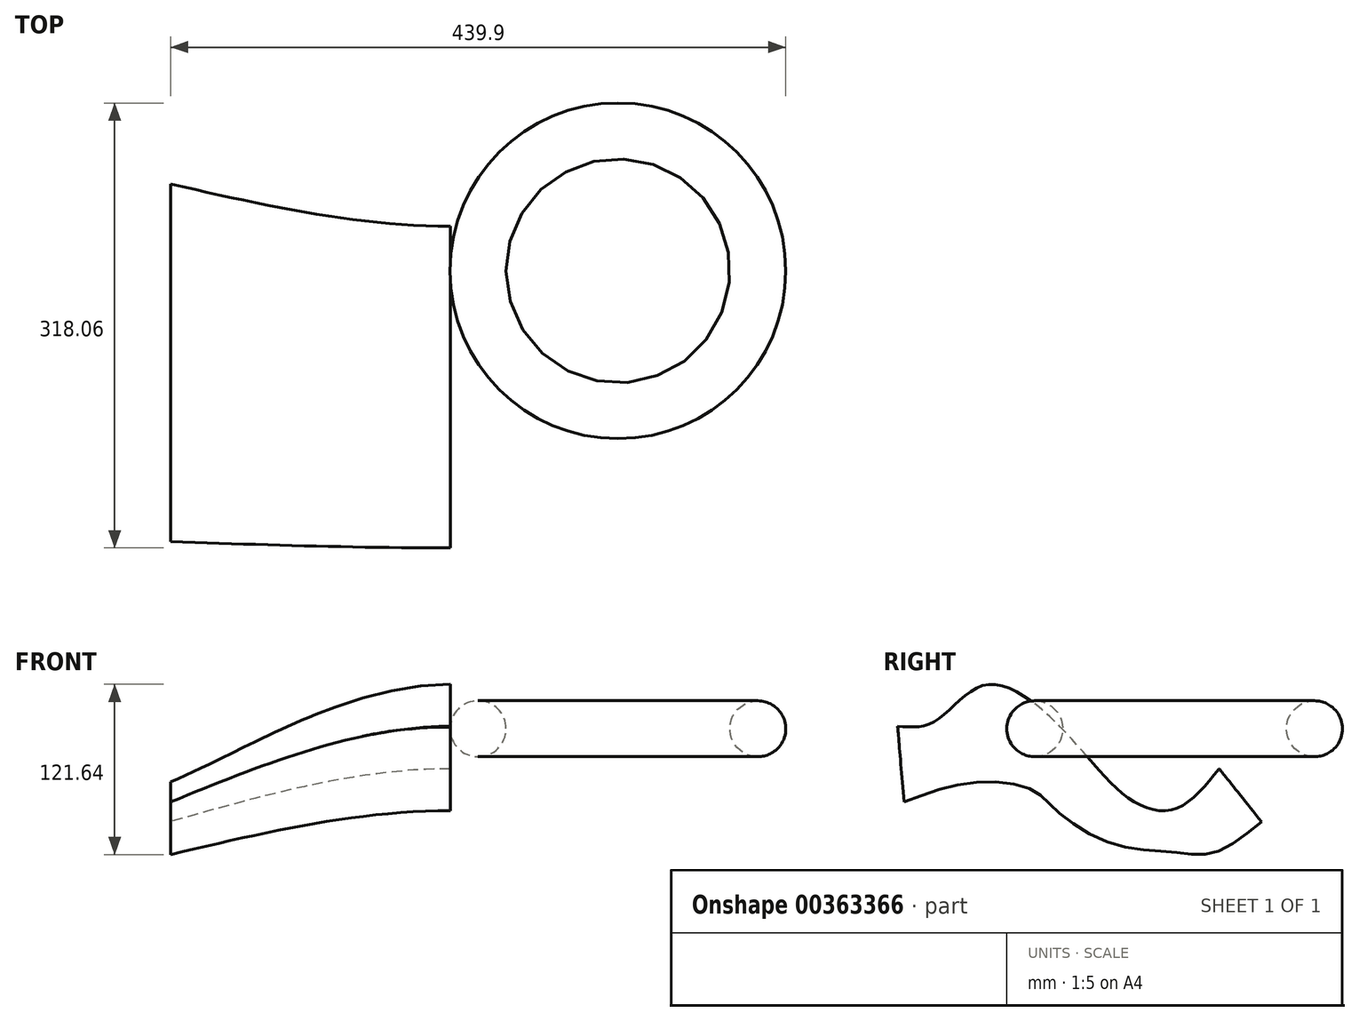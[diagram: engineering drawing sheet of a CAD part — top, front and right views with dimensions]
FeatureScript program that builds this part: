
annotation { "Feature Type Name" : "Feature", "Feature Type Description" : "" }
export const myFeature = defineFeature(function(context is Context, id is Id, definition is map)
    precondition{}
    {
        {
            var Q0;
            Q0=qCreatedBy(makeId("Front.planeOp"),FACE);
            var sketch = newSketch(context, id + "F0", { "sketchPlane" : qUnion([Q0])});
            skLineSegment(sketch, "E0.bottom", {"start": v(-40.1, 58.6) * mm, "end": v(59.9, 58.6) * mm});
            skLineSegment(sketch, "E0.top", {"start": v(-40.1, -6.4) * mm, "end": v(59.9, -6.4) * mm});
            skLineSegment(sketch, "E0.left", {"start": v(-40.1, 58.6) * mm, "end": v(-40.1, -6.4) * mm});
            skLineSegment(sketch, "E0.right", {"start": v(59.9, 58.6) * mm, "end": v(59.9, -6.4) * mm});
            skCircle(sketch, "E1", {"center": v(19.9, 28.6) * mm, "radius": 20 * mm});
            skLineSegment(sketch, "E2", {"start": v(119.9, 79.63) * mm, "end": v(119.9, -11.64) * mm, "construction": true});
            skSolve(sketch);
        }
        {
            var Q0;
            Q0=qCreatedBy(makeId("Right.planeOp"),FACE);
            var sketch = newSketch(context, id + "F1", { "sketchPlane" : qUnion([Q0])});
            skFitSpline(sketch, "E3", {"points": [v(31.85, 0) * mm, v(0, -28.73) * mm, v(-33.26, -20.8) * mm, v(-78.05, 26.03) * mm, v(-134.63, 60.07) * mm, v(-170.83, 34.26) * mm, v(-198.06, 30.31) * mm], "startDerivative": vector(-185.99, -231.7) * mm, "endDerivative": vector(-212.43, 16.55) * mm});
            skSolve(sketch);
        }
        {
            var Q0;
            Q0=sQuery(id+"F0.wireOp",EDGE,"E1");
            var Q1;
            Q1=sQuery(id+"F0.wireOp",EDGE,"E2");
            revolve(context, id + "F2", {"bodyType" : ToolBodyType.SURFACE, "surfaceEntities" : qUnion([Q0]), "axis" : qUnion([Q1]), "revolveType" : RevolveType.FULL});
        }
        {
            var Q0;
            Q0=qCreatedBy(makeId("Right.planeOp"),FACE);
            cPlane(context, id + "F3", {"entities" : qUnion([Q0]), "cplaneType" : CPlaneType.OFFSET, "offset" : 200 * mm, "oppositeDirection" : true, "width" : 150 * mm, "height" : 150 * mm});
        }
        {
            var Q0;
            Q0=qCreatedBy(id+"F3.planeOp",FACE);
            var sketch = newSketch(context, id + "F4", { "sketchPlane" : qUnion([Q0])});
            skFitSpline(sketch, "E4", {"points": [v(-193.53, -23.72) * mm, v(-145.85, -10.13) * mm, v(-101.98, -14.9) * mm, v(-84.1, -30.16) * mm, v(-43.8, -53.76) * mm, v(0, -59.72) * mm, v(27.96, -59.96) * mm, v(62.05, -37.79) * mm], "startDerivative": vector(285.5, 108.3) * mm, "endDerivative": vector(238.04, 195.8) * mm});
            skSolve(sketch);
        }
        {
            var Q0;
            Q0=sQuery(id+"F1.wireOp",EDGE,"E3");
            var Q1;
            Q1=sQuery(id+"F4.wireOp",EDGE,"E4");
            loft(context, id + "F5", {"bodyType" : ToolBodyType.SURFACE, "startCondition" : LoftEndDerivativeType.NORMAL_TO_PROFILE, "startMagnitude" : 1, "wireProfilesArray" : [{ "wireProfileEntities" : qUnion([Q0]) }, { "wireProfileEntities" : qUnion([Q1]) }]});
        }
    });
